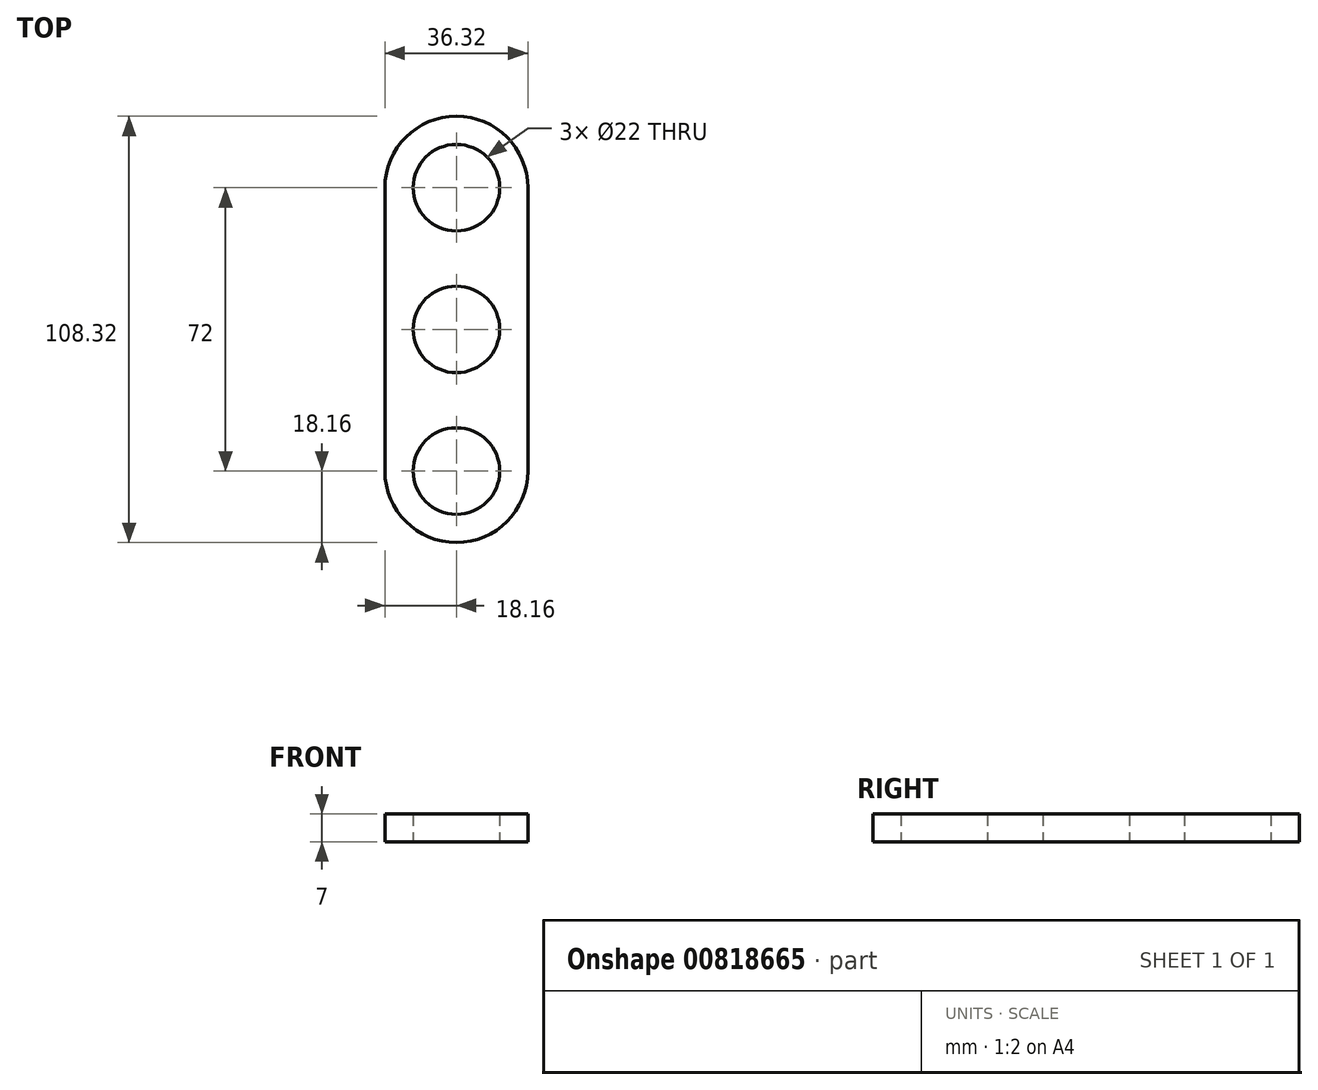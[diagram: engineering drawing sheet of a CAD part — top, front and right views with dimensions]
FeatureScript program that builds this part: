
annotation { "Feature Type Name" : "Feature", "Feature Type Description" : "" }
export const myFeature = defineFeature(function(context is Context, id is Id, definition is map)
    precondition{}
    {
        {
            var Q0;
            Q0=qCreatedBy(makeId("Top.planeOp"),FACE);
            var sketch = newSketch(context, id + "F0", { "sketchPlane" : qUnion([Q0])});
            skCircle(sketch, "E0", {"center": v(0, 0) * mm, "radius": 11 * mm});
            skLineSegment(sketch, "E1", {"start": v(-18.16, 36) * mm, "end": v(-18.16, -36) * mm});
            skLineSegment(sketch, "E2", {"start": v(18.16, 36) * mm, "end": v(18.16, -36) * mm});
            skArc(sketch, "E3", {"start": v(18.16, 36) * mm, "mid": v(0, 54.16) * mm, "end": v(-18.16, 36) * mm});
            skArc(sketch, "E4", {"start": v(-18.16, -36) * mm, "mid": v(0, -54.16) * mm, "end": v(18.16, -36) * mm});
            skCircle(sketch, "E5", {"center": v(0, -36) * mm, "radius": 11 * mm});
            skCircle(sketch, "E6", {"center": v(0, 36) * mm, "radius": 11 * mm});
            skSolve(sketch);
        }
        {
            var Q0;
            Q0 = qSketchRegion(id + "F0", true);
            extrude(context, id + "F1", {"entities" : qUnion([Q0]), "depth" : 7 * mm, "offsetDistance" : 25 * mm});
        }
    });
